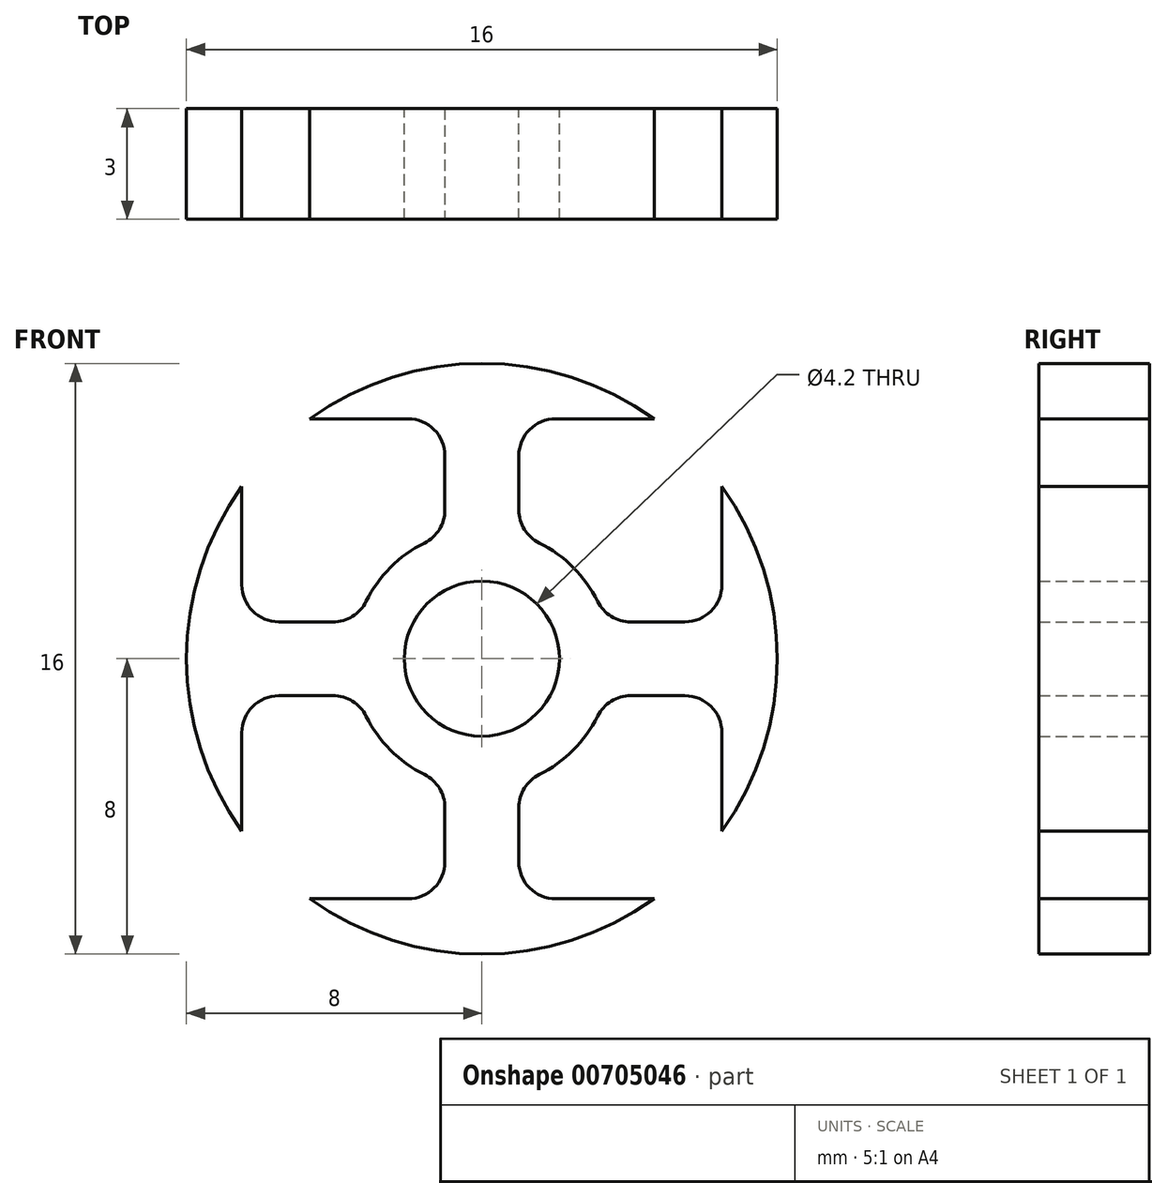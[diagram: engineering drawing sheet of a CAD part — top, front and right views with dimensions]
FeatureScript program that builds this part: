
annotation { "Feature Type Name" : "Feature", "Feature Type Description" : "" }
export const myFeature = defineFeature(function(context is Context, id is Id, definition is map)
    precondition{}
    {
        {
            var Q0;
            Q0=qCreatedBy(makeId("Front.planeOp"),FACE);
            var sketch = newSketch(context, id + "F0", { "sketchPlane" : qUnion([Q0])});
            skArc(sketch, "E0", {"start": v(-6.5, 4.66) * mm, "mid": v(-8, 0) * mm, "end": v(-6.5, -4.66) * mm});
            skCircle(sketch, "E1", {"center": v(0, 0) * mm, "radius": 3.5 * mm});
            skCircle(sketch, "E2", {"center": v(0, 0) * mm, "radius": 2.1 * mm});
            skLineSegment(sketch, "E3.bottom", {"start": v(4.66, -6.5) * mm, "end": v(-4.66, -6.5) * mm});
            skLineSegment(sketch, "E3.top", {"start": v(4.66, 6.5) * mm, "end": v(-4.66, 6.5) * mm});
            skLineSegment(sketch, "E3.left", {"start": v(6.5, -4.66) * mm, "end": v(6.5, 4.66) * mm});
            skLineSegment(sketch, "E3.right", {"start": v(-6.5, -4.66) * mm, "end": v(-6.5, 4.66) * mm});
            skLineSegment(sketch, "E4.bottom", {"start": v(0, 0) * mm, "end": v(-6.5, 0) * mm});
            skLineSegment(sketch, "E4.top", {"start": v(0, 1) * mm, "end": v(-6.5, 1) * mm});
            skLineSegment(sketch, "E4.left", {"start": v(0, 0) * mm, "end": v(0, 1) * mm});
            skLineSegment(sketch, "E4.right", {"start": v(-6.5, 0) * mm, "end": v(-6.5, 1) * mm});
            skLineSegment(sketch, "E5.top", {"start": v(0, -1) * mm, "end": v(-6.5, -1) * mm});
            skLineSegment(sketch, "E5.left", {"start": v(0, 0) * mm, "end": v(0, -1) * mm});
            skLineSegment(sketch, "E5.right", {"start": v(-6.5, 0) * mm, "end": v(-6.5, -1) * mm});
            skLineSegment(sketch, "E6.bottom", {"start": v(0, 0) * mm, "end": v(1, 0) * mm});
            skLineSegment(sketch, "E6.top", {"start": v(0, 6.5) * mm, "end": v(1, 6.5) * mm});
            skLineSegment(sketch, "E6.left", {"start": v(0, 0) * mm, "end": v(0, 6.5) * mm});
            skLineSegment(sketch, "E6.right", {"start": v(1, 0) * mm, "end": v(1, 6.5) * mm});
            skLineSegment(sketch, "E7.bottom", {"start": v(0, 0) * mm, "end": v(-1, 0) * mm});
            skLineSegment(sketch, "E7.top", {"start": v(0, 6.5) * mm, "end": v(-1, 6.5) * mm});
            skLineSegment(sketch, "E7.right", {"start": v(-1, 0) * mm, "end": v(-1, 6.5) * mm});
            skLineSegment(sketch, "E8.top", {"start": v(0, -6.5) * mm, "end": v(1, -6.5) * mm});
            skLineSegment(sketch, "E8.left", {"start": v(0, 0) * mm, "end": v(0, -6.5) * mm});
            skLineSegment(sketch, "E8.right", {"start": v(1, 0) * mm, "end": v(1, -6.5) * mm});
            skLineSegment(sketch, "E9.top", {"start": v(0, -6.5) * mm, "end": v(-1, -6.5) * mm});
            skLineSegment(sketch, "E9.right", {"start": v(-1, 0) * mm, "end": v(-1, -6.5) * mm});
            skPoint(sketch, "E10.orphan", {"position": v(-6.5, 6.5) * mm});
            skPoint(sketch, "E11.orphan", {"position": v(-6.5, -6.5) * mm});
            skArc(sketch, "E12.trimOffspring", {"start": v(-4.66, -6.5) * mm, "mid": v(0, -8) * mm, "end": v(4.66, -6.5) * mm});
            skPoint(sketch, "E13.orphan", {"position": v(6.5, -6.5) * mm});
            skLineSegment(sketch, "E14.bottom", {"start": v(0, 0) * mm, "end": v(6.5, 0) * mm});
            skLineSegment(sketch, "E14.top", {"start": v(0, 1) * mm, "end": v(6.5, 1) * mm});
            skLineSegment(sketch, "E14.right", {"start": v(6.5, 0) * mm, "end": v(6.5, 1) * mm});
            skLineSegment(sketch, "E15.top", {"start": v(0, -1) * mm, "end": v(6.5, -1) * mm});
            skLineSegment(sketch, "E15.right", {"start": v(6.5, 0) * mm, "end": v(6.5, -1) * mm});
            skArc(sketch, "E16.trimOffspring", {"start": v(6.5, -4.66) * mm, "mid": v(8, 0) * mm, "end": v(6.5, 4.66) * mm});
            skPoint(sketch, "E17.orphan", {"position": v(6.5, 6.5) * mm});
            skArc(sketch, "E18.trimOffspring", {"start": v(4.66, 6.5) * mm, "mid": v(0, 8) * mm, "end": v(-4.66, 6.5) * mm});
            skSolve(sketch);
        }
        {
            var Q0;
            Q0 = qSketchRegion(id + "F0", true);
            extrude(context, id + "F1", {"entities" : qUnion([Q0]), "depth" : 3 * mm, "offsetDistance" : 25 * mm});
        }
        {
            var Q0;
            Q0=makeQuery(id+"F1.opExtrude","SWEPT_EDGE",EDGE,{"disambiguationData":[OSD([sQuery(id+"F0.wireOp",EDGE,"E3.bottom"),sQuery(id+"F0.wireOp",EDGE,"E9.top"),sQuery(id+"F0.wireOp",EDGE,"E9.right")])]});
            var Q1;
            Q1=makeQuery(id+"F1.opExtrude","SWEPT_EDGE",EDGE,{"disambiguationData":[OSD([sQuery(id+"F0.wireOp",EDGE,"E1"),sQuery(id+"F0.wireOp",EDGE,"E4.top")])]});
            var Q2;
            Q2=makeQuery(id+"F1.opExtrude","SWEPT_EDGE",EDGE,{"disambiguationData":[OSD([sQuery(id+"F0.wireOp",EDGE,"E1"),sQuery(id+"F0.wireOp",EDGE,"E7.right")])]});
            var Q3;
            Q3=makeQuery(id+"F1.opExtrude","SWEPT_EDGE",EDGE,{"disambiguationData":[OSD([sQuery(id+"F0.wireOp",EDGE,"E3.left"),sQuery(id+"F0.wireOp",EDGE,"E14.top"),sQuery(id+"F0.wireOp",EDGE,"E14.right")])]});
            var Q4;
            Q4=makeQuery(id+"F1.opExtrude","SWEPT_EDGE",EDGE,{"disambiguationData":[OSD([sQuery(id+"F0.wireOp",EDGE,"E1"),sQuery(id+"F0.wireOp",EDGE,"E15.top")])]});
            var Q5;
            Q5=makeQuery(id+"F1.opExtrude","SWEPT_EDGE",EDGE,{"disambiguationData":[OSD([sQuery(id+"F0.wireOp",EDGE,"E1"),sQuery(id+"F0.wireOp",EDGE,"E8.right")])]});
            var Q6;
            Q6=makeQuery(id+"F1.opExtrude","SWEPT_EDGE",EDGE,{"disambiguationData":[OSD([sQuery(id+"F0.wireOp",EDGE,"E3.right"),sQuery(id+"F0.wireOp",EDGE,"E5.top"),sQuery(id+"F0.wireOp",EDGE,"E5.right")])]});
            var Q7;
            Q7=makeQuery(id+"F1.opExtrude","SWEPT_EDGE",EDGE,{"disambiguationData":[OSD([sQuery(id+"F0.wireOp",EDGE,"E3.top"),sQuery(id+"F0.wireOp",EDGE,"E6.top"),sQuery(id+"F0.wireOp",EDGE,"E6.right")])]});
            var Q8;
            Q8=makeQuery(id+"F1.opExtrude","SWEPT_EDGE",EDGE,{"disambiguationData":[OSD([sQuery(id+"F0.wireOp",EDGE,"E3.left"),sQuery(id+"F0.wireOp",EDGE,"E15.top"),sQuery(id+"F0.wireOp",EDGE,"E15.right")])]});
            var Q9;
            Q9=makeQuery(id+"F1.opExtrude","SWEPT_EDGE",EDGE,{"disambiguationData":[OSD([sQuery(id+"F0.wireOp",EDGE,"E1"),sQuery(id+"F0.wireOp",EDGE,"E9.right")])]});
            var Q10;
            Q10=makeQuery(id+"F1.opExtrude","SWEPT_EDGE",EDGE,{"disambiguationData":[OSD([sQuery(id+"F0.wireOp",EDGE,"E1"),sQuery(id+"F0.wireOp",EDGE,"E5.top")])]});
            var Q11;
            Q11=makeQuery(id+"F1.opExtrude","SWEPT_EDGE",EDGE,{"disambiguationData":[OSD([sQuery(id+"F0.wireOp",EDGE,"E3.right"),sQuery(id+"F0.wireOp",EDGE,"E4.top"),sQuery(id+"F0.wireOp",EDGE,"E4.right")])]});
            var Q12;
            Q12=makeQuery(id+"F1.opExtrude","SWEPT_EDGE",EDGE,{"disambiguationData":[OSD([sQuery(id+"F0.wireOp",EDGE,"E1"),sQuery(id+"F0.wireOp",EDGE,"E6.right")])]});
            var Q13;
            Q13=makeQuery(id+"F1.opExtrude","SWEPT_EDGE",EDGE,{"disambiguationData":[OSD([sQuery(id+"F0.wireOp",EDGE,"E1"),sQuery(id+"F0.wireOp",EDGE,"E14.top")])]});
            var Q14;
            Q14=makeQuery(id+"F1.opExtrude","SWEPT_EDGE",EDGE,{"disambiguationData":[OSD([sQuery(id+"F0.wireOp",EDGE,"E3.top"),sQuery(id+"F0.wireOp",EDGE,"E7.top"),sQuery(id+"F0.wireOp",EDGE,"E7.right")])]});
            var Q15;
            Q15=makeQuery(id+"F1.opExtrude","SWEPT_EDGE",EDGE,{"disambiguationData":[OSD([sQuery(id+"F0.wireOp",EDGE,"E3.bottom"),sQuery(id+"F0.wireOp",EDGE,"E8.top"),sQuery(id+"F0.wireOp",EDGE,"E8.right")])]});
            fillet(context, id + "F2", {"entities" : qUnion([Q0, Q1, Q2, Q3, Q4, Q5, Q6, Q7, Q8, Q9, Q10, Q11, Q12, Q13, Q14, Q15]), "radius" : 1 * mm, "tangentPropagation" : true, "allowEdgeOverflow" : false});
        }
    });
